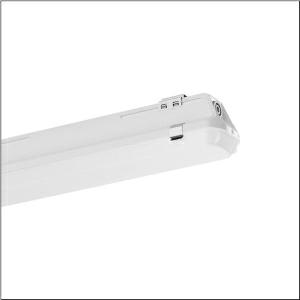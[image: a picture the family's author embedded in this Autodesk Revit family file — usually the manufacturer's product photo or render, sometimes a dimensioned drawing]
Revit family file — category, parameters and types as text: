
# Revit family: monsun_r__11_51fp12mp480h_cfdd
name_source: partatom
category: Lighting Fixtures
units: mm (PartAtom-declared; Revit-internal decimal feet)

## family parameters
Cut with Voids When Loaded = No
Host = Face
Light Source = No
Part Type = Normal
Room Calculation Point = No
Round Connector Dimension = Use Diameter
Shared = No

## types (1)
- --- (1 x LED, 7990 lm, 45.4 W, 4000K)
    Apparent Load = 45 VA
    CIE Flux Codes = 65 88 97 97 100
    Color Rendering = 80
    Color Temperature = 4000K
    Default Elevation = 1800 mm
    Description = Monsun® 11, damp-proof luminaire, chain hanger, primary light control with lens, primary optical cover: enclosure, of PMMA, light emission: direct distribution, primary light characteristic: symmetric, installation type: suspended mounting, surface-mounted, horizontal mounting, vertical mounting, LED, rated luminous flux: 7.990lm, luminous efficacy: 176lm/W, light colour: 840, colour temperature: 4000K, control gear: ECG, with terminal, 3-pole, max. 2.5mm², mains connection: 220..240V, AC, 50/60Hz, rated input power: 45W, luminaire housing, of glass-fibre reinforced polyester, uncoated, bright grey, incl. chain hanger, length: 1.590mm, width: 90mm, height: 88mm, clip for enclosure, of stainless steel (V2A), ceiling mounting element, of stainless steel (V2A), chain hanger, of stainless steel (V2A), protection rating (complete): IP66, insulation class (complete): insulation class I (protective earthing), certification: CE, ENEC, VDE, UKCA, protection symbol: D, impact resistance: IK04, permissible operating ambient temperature: -35..+40°C, standard: EN 50419, EN 60598-2-1, no direct snow, no direct sun, no direct rain, for indoor or canopied outdoor use, corresponds to IFS (International Featured Standards) requirements for safety and quality in the food industry, contact your sales advisor before using the luminaires in applications with unclear chemical exposure, large temperature fluctuations or condensation-forming humidity, LABS conformity tested according to VDMA 24364:2018-05, packaging unit: 1 piece
    Height = 89 mm
    Lamp = 1 x LED
    Lamp Light Flux = 7990 lm
    Lamp Power = 45.4 W
    Lamp count = 1
    Length = 1590 mm
    Luminous efficacy = 176 lm/W
    Manufacturer = Siteco
    ModVariant = No
    Model = 51FP12MP480H
    Mounting Place = Ceiling
    Mounting Type = Surface mounted
    Number of Poles = 1
    OnlyDefault = Yes
    Power Factor = 1
    Product Name = Monsun® 11
    Product group = damp-proof luminaire
    ProductGroupID = 300
    Protection Class = Protection class I
    Protection Degree = IP 66
    RLX_Detail_Level = 1
    RLX_Emergency_Light_Flux = 0 lm
    RLX_Emergency_Type = 0
    RLX_Emergency_Type_DB = No
    RlxData = <blob elided: 90205 chars, md5=aaf33d0e>
    Socket = socket
    Standby Power = 0 W
    System Light Flux = 7990 lm
    System Power = 45 W
    Type Comments = factory setting: luminous flux: 100 % | (A | C | E) | 105 mA
    Type Image = l_1004748.jpg
    URL = http://relux.com
    VarID = @adj_142109
    Voltage = 0 V
    Weight = 0.00 kg
    Width = 90 mm

## geometry (parser evidence)
native form markers: Blend x4, Sweep x10
no freeform markers — native parametric forms only
